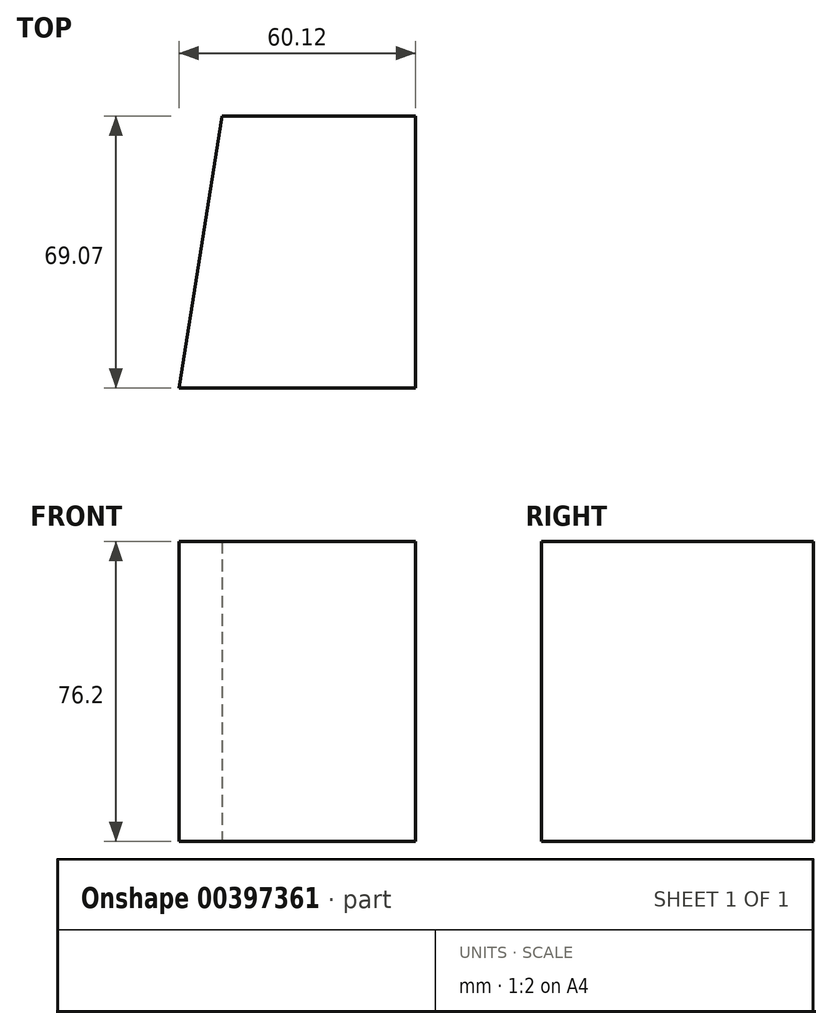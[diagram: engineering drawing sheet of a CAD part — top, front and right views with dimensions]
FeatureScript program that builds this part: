
annotation { "Feature Type Name" : "Feature", "Feature Type Description" : "" }
export const myFeature = defineFeature(function(context is Context, id is Id, definition is map)
    precondition{}
    {
        {
            var Q0;
            Q0=qCreatedBy(makeId("Top.planeOp"),FACE);
            var sketch = newSketch(context, id + "F0", { "sketchPlane" : qUnion([Q0])});
            skLineSegment(sketch, "E0", {"start": v(0, 0) * mm, "end": v(60.12, 0) * mm});
            skLineSegment(sketch, "E1", {"start": v(60.12, 0) * mm, "end": v(60.12, 69.07) * mm});
            skLineSegment(sketch, "E2", {"start": v(60.12, 69.07) * mm, "end": v(10.9, 69.07) * mm});
            skLineSegment(sketch, "E3", {"start": v(10.9, 69.07) * mm, "end": v(0, 0) * mm});
            skSolve(sketch);
        }
        {
            var Q0;
            Q0=makeQuery(id+"F0.imprint","IMPRINT",FACE,{"disambiguationData":[TD([[makeQuery(id+"F0.imprint","IMPRINT",EDGE,{"derivedFrom":sQuery(id+"F0.wireOp",EDGE,"E0")}),1.0]])]});
            extrude(context, id + "F1", {"entities" : qUnion([Q0]), "depth" : 76.2 * mm});
        }
    });
